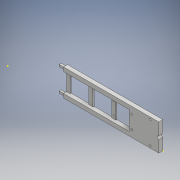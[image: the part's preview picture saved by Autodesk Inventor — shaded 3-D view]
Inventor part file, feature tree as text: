
AUTODESK INVENTOR PART (.ipt)
format: ipt  version: 2018 (Build 220112000, 112)  size: 645,632 bytes
history: native  units: mm
features: sketch x35, extrude x27, hole x6, fillet x6
ambient origin geometry x8: Origin, YZ Plane, XZ Plane, XY Plane, X Axis, Y Axis, Z Axis, Center Point
bodies: Solid1 (feature_tree)
feature tree (74):
  extrude  "Extrusion1"  Depth=50.0mm
  hole  "Hole1"  [1 undecoded]
  hole  "Hole2"  [1 undecoded]
  extrude  "Extrusion2"  Depth=25.0mm
  extrude  "Extrusion3"  Depth=25.0mm
  extrude  "Extrusion4"  Depth=5.0mm
  sketch  "Sketch7"  dims[d25=10.0mm d26=5.0mm]
  extrude  "Extrusion5"  Depth=5.0mm
  extrude  "Extrusion6"  Depth=35.0mm
  extrude  "Extrusion7"  Depth=35.0mm
  extrude  "Extrusion8"  Depth=35.0mm
  extrude  "Extrusion9"  Depth=2.0mm TaperAngle=0.0deg
  extrude  "Extrusion10"  Depth=7.5mm TaperAngle=0.0deg
  extrude  "Extrusion11"  Depth=10.0mm
  extrude  "Extrusion12"  Depth=7.5mm
  fillet  "Fillet1"  Radius=7.5mm
  fillet  "Fillet2"  Radius=25.0mm
  fillet  "Fillet3"  Radius=3.0mm
  fillet  "Fillet4"  Radius=3.2mm
  fillet  "Fillet5"  Radius=2.1mm
  fillet  "Fillet6"  Radius=5.5mm
  extrude  "Extrusion13"  Depth=92.5mm TaperAngle=0.0deg
  sketch  "Sketch17"  dims[d58=4.25mm d59=241.0mm d60=0.0mm]
  hole  "Hole3"  [1 undecoded]
  hole  "Hole4"  [1 undecoded]
  extrude  "Extrusion14"  Depth=5.0mm
  extrude  "Extrusion15"  Depth=91.25mm TaperAngle=0.0deg
  extrude  "Extrusion16"  Depth=30.0mm
  extrude  "Extrusion17"  Depth=2.5mm
  extrude  "Extrusion18"  Depth=14.55mm TaperAngle=0.0deg
  extrude  "Extrusion19"  Depth=0.1mm
  extrude  "Extrusion20"  Depth=3.25mm
  extrude  "Extrusion21"  Depth=3.25mm
  hole  "Hole5"  [1 undecoded]
  extrude  "Extrusion22"  Depth=2.0mm
  extrude  "Extrusion23"  Depth=15.0mm
  extrude  "Extrusion24"  Depth=10.0mm TaperAngle=0.0deg
  hole  "Hole6"  [1 undecoded]
  extrude  "Extrusion25"  Depth=100.0mm TaperAngle=0.0deg
  extrude  "Extrusion26"  Depth=2.0mm TaperAngle=0.0deg
  extrude  "Extrusion27"  Depth=10.0mm
  sketch  "Sketch1"  dims[d0=50.0mm d1=50.0mm]
  sketch  "Sketch2"  dims[d2=240.0mm d3=7.5mm]
  sketch  "Sketch3"  dims[d4=7.5mm d5=7.5mm d6=0.0mm]
  sketch  "Sketch4"  dims[d7=6.35mm d8=6.0mm d9=4.0mm d10=2.0mm d11=90.0deg d12=8.0mm d13=20.594885mm d14=25.0mm]
  sketch  "Sketch5"  dims[d15=3.3mm d16=6.0mm d17=4.0mm d18=2.0mm d19=90.0deg d20=8.0mm d21=20.594885mm d22=25.0mm]
  sketch  "Sketch6"  dims[d23=180.0deg d24=5.0mm]
  sketch  "Sketch8"  dims[d27=17.5mm d28=0.0mm d30=35.0mm]
  sketch  "Sketch9"  dims[d31=35.0mm d32=35.0mm]
  sketch  "Sketch10"  dims[d33=35.0mm d34=35.0mm]
  sketch  "Sketch11"  dims[d35=35.0mm d36=2.0mm d37=0.0mm]
  sketch  "Sketch12"  dims[d38=10.0mm d39=7.5mm d40=0.0mm]
  sketch  "Sketch13"  dims[d41=100.0mm d42=10.0mm]
  sketch  "Sketch14"  dims[d43=7.5mm d44=0.0mm d45=7.5mm d46=7.5mm d47=25.0mm d48=0.0mm d49=3.0mm d50=3.2mm d51=2.1mm d52=5.5mm]
  sketch  "Sketch15"  dims[d53=3.3mm d54=92.5mm d55=0.0mm]
  sketch  "Sketch16"  dims[d56=5.5mm d57=3.3mm]
  sketch  "Sketch18"  dims[d61=4.44mm d62=5.0mm]
  sketch  "Sketch19"  dims[d63=2.5mm d64=91.25mm d65=0.0mm]
  sketch  "Sketch20"  dims[d66=30.0mm d67=6.35mm]
  sketch  "Sketch21"  dims[d68=3.8mm d69=0.0mm d70=2.5mm]
  sketch  "Sketch22"  dims[d71=14.55mm d72=0.0mm d73=14.55mm d74=0.0mm]
  sketch  "Sketch23"  dims[d75=0.1mm d76=0.1mm]
  sketch  "Sketch24"  dims[d77=3.25mm d78=3.25mm]
  sketch  "Sketch25"  dims[d79=3.25mm d80=3.25mm]
  sketch  "Sketch26"  dims[d81=35.0mm d82=10.0mm]
  sketch  "Sketch27"  dims[d83=2.0mm d84=0.0mm d85=3.6mm]
  sketch  "Sketch28"  dims[d86=3.6mm]
  sketch  "Sketch29"  dims[d87=3.3mm d88=6.0mm d89=4.0mm d90=2.0mm d91=90.0deg d92=15.0mm d93=20.594885mm]
  sketch  "Sketch30"  dims[d94=3.3mm d95=6.0mm d96=4.0mm d97=2.0mm d98=90.0deg d99=15.0mm d100=20.594885mm d101=6.0mm]
  sketch  "Sketch31"  dims[d102=20.0mm d103=0.0mm d104=10.0mm d105=0.0mm]
  sketch  "Sketch32"  dims[d106=2.0mm d107=0.0mm d108=4.0mm]
  sketch  "Sketch33"  dims[d109=100.0mm d110=0.0mm d111=100.0mm d112=0.0mm]
  sketch  "Sketch34"  dims[d113=5.0mm d114=2.0mm d115=0.0mm]
  sketch  "Sketch35"  dims[d116=3.3mm d117=3.3mm d118=3.3mm d119=3.3mm d120=2.0mm d121=0.0mm d122=5.5mm d123=0.0mm d124=3.3mm d125=6.0mm d126=4.0mm d127=2.0mm d128=90.0deg d129=8.0mm d130=20.594885mm d131=42.0mm d132=17.0mm d133=21.0mm d135=8.5mm d136=15.825mm d137=3.5mm d138=21.0mm d139=3.3mm d140=3.3mm d141=3.3mm d142=10.0mm d143=0.0mm d144=7.5mm d145=0.0mm d146=5.0mm d147=10.0mm d148=5.0mm d149=10.0mm d150=17.5mm d151=0.0mm d152=5.0mm d153=7.0mm d154=6.0mm d155=4.0mm d156=2.0mm d157=90.0deg d158=8.0mm d159=20.594885mm d160=17.5mm d161=0.0mm d162=170.5mm d163=0.0mm d164=3.75mm d165=3.75mm d166=3.75mm d167=3.75mm d168=10.0mm d169=0.0mm]
note: 6 required parameter values undecoded (feature->parameter linkage not recoverable at this tier; creation-order binding heuristic only, values carry confidence <= 0.55)
